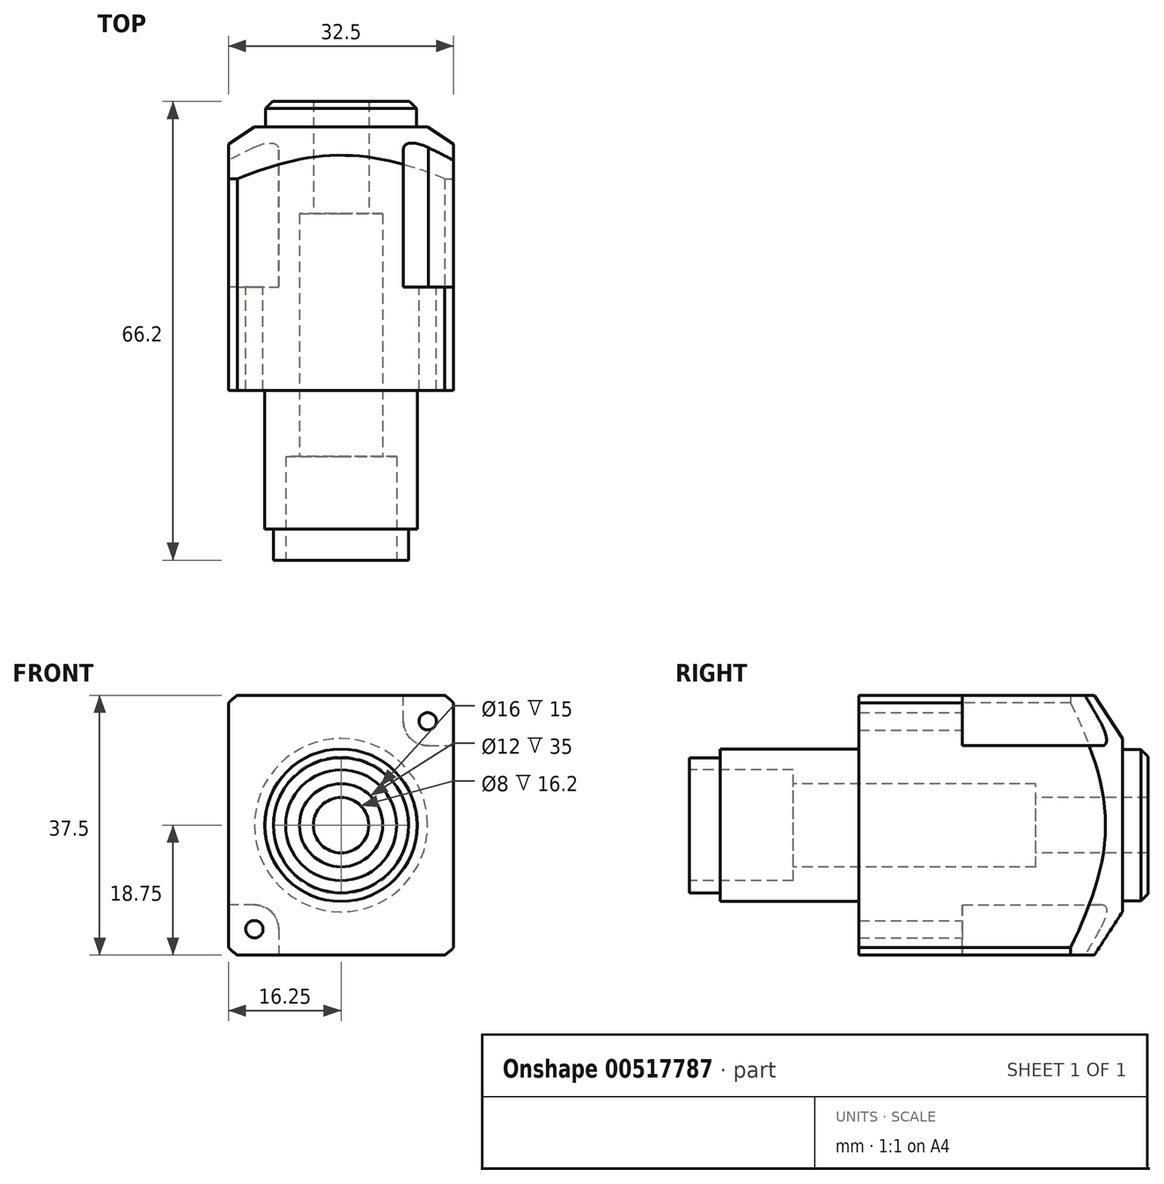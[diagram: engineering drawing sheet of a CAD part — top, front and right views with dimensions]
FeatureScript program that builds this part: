
annotation { "Feature Type Name" : "Feature", "Feature Type Description" : "" }
export const myFeature = defineFeature(function(context is Context, id is Id, definition is map)
    precondition{}
    {
        {
            var Q0;
            Q0=qCreatedBy(makeId("Right.planeOp"),FACE);
            var sketch = newSketch(context, id + "F0", { "sketchPlane" : qUnion([Q0])});
            skLineSegment(sketch, "E0", {"start": v(4.5, 11) * mm, "end": v(24.5, 11) * mm});
            skLineSegment(sketch, "E1", {"start": v(24.5, 24) * mm, "end": v(24.5, 11) * mm});
            skLineSegment(sketch, "E2", {"start": v(24.5, 24) * mm, "end": v(55.03, 24) * mm});
            skLineSegment(sketch, "E3", {"start": v(55.03, 24) * mm, "end": v(62.5, 12.5) * mm});
            skLineSegment(sketch, "E4", {"start": v(66.2, 4) * mm, "end": v(50, 4) * mm});
            skLineSegment(sketch, "E5", {"start": v(50, 4) * mm, "end": v(50, 6) * mm});
            skLineSegment(sketch, "E6", {"start": v(50, 6) * mm, "end": v(15, 6) * mm});
            skLineSegment(sketch, "E7", {"start": v(15, 6) * mm, "end": v(15, 8) * mm});
            skLineSegment(sketch, "E8", {"start": v(15, 8) * mm, "end": v(0, 8) * mm});
            skLineSegment(sketch, "E9", {"start": v(0, 9.75) * mm, "end": v(0, 8) * mm});
            skLineSegment(sketch, "E10", {"start": v(0, 0) * mm, "end": v(89.53, 0) * mm});
            skLineSegment(sketch, "E11", {"start": v(4.5, 11) * mm, "end": v(4.5, 9.75) * mm});
            skPoint(sketch, "E12.orphan", {"position": v(0, 11) * mm});
            skLineSegment(sketch, "E13", {"start": v(66.2, 10.9) * mm, "end": v(66.2, 4) * mm});
            skLineSegment(sketch, "E14", {"start": v(62.5, 12.5) * mm, "end": v(62.5, 10.9) * mm});
            skLineSegment(sketch, "E15", {"start": v(66.2, 10.9) * mm, "end": v(62.5, 10.9) * mm});
            skLineSegment(sketch, "E16", {"start": v(0, 9.75) * mm, "end": v(4.5, 9.75) * mm});
            skSolve(sketch);
        }
        {
            var Q0;
            Q0=makeQuery(id+"F0.imprint","IMPRINT",FACE,{"disambiguationData":[TD([[makeQuery(id+"F0.imprint","IMPRINT",EDGE,{"derivedFrom":sQuery(id+"F0.wireOp",EDGE,"E0")}),-1.0]])]});
            var Q1;
            Q1=sQuery(id+"F0.wireOp",EDGE,"E10");
            revolve(context, id + "F1", {"entities" : qUnion([Q0]), "axis" : qUnion([Q1]), "revolveType" : RevolveType.FULL});
        }
        {
            var Q0;
            Q0=makeQuery(id+"F1.opRevolve","SWEPT_FACE",FACE,{"disambiguationData":[OSD([sQuery(id+"F0.wireOp",EDGE,"E13")])]});
            var sketch = newSketch(context, id + "F2", { "sketchPlane" : qUnion([Q0])});
            skLineSegment(sketch, "E17.bottom", {"start": v(-16.25, 18.75) * mm, "end": v(16.25, 18.75) * mm});
            skLineSegment(sketch, "E17.top", {"start": v(-16.25, -18.75) * mm, "end": v(16.25, -18.75) * mm});
            skLineSegment(sketch, "E17.left", {"start": v(-16.25, 18.75) * mm, "end": v(-16.25, -18.75) * mm});
            skLineSegment(sketch, "E17.right", {"start": v(16.25, 18.75) * mm, "end": v(16.25, -18.75) * mm});
            skLineSegment(sketch, "E18.bottom", {"start": v(-37.96, 36.73) * mm, "end": v(41.17, 36.73) * mm});
            skLineSegment(sketch, "E18.top", {"start": v(-37.96, -41.68) * mm, "end": v(41.17, -41.68) * mm});
            skLineSegment(sketch, "E18.left", {"start": v(-37.96, 36.73) * mm, "end": v(-37.96, -41.68) * mm});
            skLineSegment(sketch, "E18.right", {"start": v(41.17, 36.73) * mm, "end": v(41.17, -41.68) * mm});
            skSolve(sketch);
        }
        {
            var Q0;
            Q0 = qSketchRegion(id + "F2", true);
            extrude(context, id + "F3", {"entities" : qUnion([Q0]), "operationType" : NewBodyOperationType.REMOVE, "endBound" : BoundingType.THROUGH_ALL, "oppositeDirection" : true, "depth" : 25 * mm, "offsetDistance" : 25 * mm});
        }
        {
            var Q0;
            Q0=makeQuery(id+"F1.opRevolve","SWEPT_FACE",FACE,{"disambiguationData":[OSD([sQuery(id+"F0.wireOp",EDGE,"E13")])]});
            var sketch = newSketch(context, id + "F4", { "sketchPlane" : qUnion([Q0])});
            skArc(sketch, "E19", {"start": v(-12.6, 11.5) * mm, "mid": v(-10.06, 12.5) * mm, "end": v(-9, 15) * mm});
            skLineSegment(sketch, "E20", {"start": v(-9, 15) * mm, "end": v(-9, 21) * mm});
            skLineSegment(sketch, "E21", {"start": v(-9, 21) * mm, "end": v(-18, 21) * mm});
            skLineSegment(sketch, "E22", {"start": v(-18, 21) * mm, "end": v(-18, 11.5) * mm});
            skLineSegment(sketch, "E23", {"start": v(-12.6, 11.5) * mm, "end": v(-18, 11.5) * mm});
            skArc(sketch, "E24", {"start": v(12.5, -11.5) * mm, "mid": v(10.03, -12.53) * mm, "end": v(9, -15) * mm});
            skLineSegment(sketch, "E25", {"start": v(12.5, -11.5) * mm, "end": v(18, -11.5) * mm});
            skLineSegment(sketch, "E26", {"start": v(18, -11.5) * mm, "end": v(18, -21) * mm});
            skLineSegment(sketch, "E27", {"start": v(18, -21) * mm, "end": v(9, -21) * mm});
            skLineSegment(sketch, "E28", {"start": v(9, -15) * mm, "end": v(9, -21) * mm});
            skPoint(sketch, "E29.orphan", {"position": v(8.56, -21) * mm});
            skSolve(sketch);
        }
        {
            var Q0;
            Q0 = qSketchRegion(id + "F4", true);
            extrude(context, id + "F5", {"entities" : qUnion([Q0]), "operationType" : NewBodyOperationType.REMOVE, "oppositeDirection" : true, "depth" : 26.8 * mm, "offsetDistance" : 25 * mm});
        }
        {
            var Q0;
            Q0=makeQuery(id+"F5.boolean.opBoolean","COPY",FACE,{"derivedFrom":makeQuery(id+"F5.opExtrude","CAP_FACE",FACE,{"disambiguationData":[OSD([sQuery(id+"F4.wireOp",EDGE,"E24"),sQuery(id+"F4.wireOp",EDGE,"E25"),sQuery(id+"F4.wireOp",EDGE,"E26"),sQuery(id+"F4.wireOp",EDGE,"E27"),sQuery(id+"F4.wireOp",EDGE,"E28")])],"isStart":false})});
            var sketch = newSketch(context, id + "F6", { "sketchPlane" : qUnion([Q0])});
            skPoint(sketch, "E30", {"position": v(-12.5, 15) * mm});
            skPoint(sketch, "E31", {"position": v(12.5, -15) * mm});
            skSolve(sketch);
        }
        {
            var Q0;
            Q0=sQuery(id+"F6.wireOp",VERTEX,"E30");
            var Q1;
            Q1=sQuery(id+"F6.wireOp",VERTEX,"E31");
            var Q2;
            Q2=makeQuery(id+"F1.opRevolve","SWEPT_BODY",BODY,{"disambiguationData":[OSD([sQuery(id+"F0.wireOp",EDGE,"E0"),sQuery(id+"F0.wireOp",EDGE,"E1"),sQuery(id+"F0.wireOp",EDGE,"E2"),sQuery(id+"F0.wireOp",EDGE,"E3"),sQuery(id+"F0.wireOp",EDGE,"E4"),sQuery(id+"F0.wireOp",EDGE,"E5"),sQuery(id+"F0.wireOp",EDGE,"E6"),sQuery(id+"F0.wireOp",EDGE,"E7"),sQuery(id+"F0.wireOp",EDGE,"E8"),sQuery(id+"F0.wireOp",EDGE,"E9"),sQuery(id+"F0.wireOp",EDGE,"TxGgKCIe-eiSN-omVE-WW9B-d0bGM8mBuf6P"),sQuery(id+"F0.wireOp",EDGE,"E11"),sQuery(id+"F0.wireOp",EDGE,"E13"),sQuery(id+"F0.wireOp",EDGE,"E14"),sQuery(id+"F0.wireOp",EDGE,"E15")])]});
            hole(context, id + "F7", {"style" : HoleStyle.SIMPLE, "endStyle" : HoleEndStyle.BLIND, "holeDiameter" : 2.5 * mm, "holeDepth" : 50 * mm, "isTappedThrough" : true, "tappedDepth" : 12 * mm, "tapClearance" : 3, "startFromSketch" : true, "locations" : qUnion([Q0, Q1]), "scope" : qUnion([Q2])});
        }
        {
            var Q0;
            Q0=makeQuery(id+"F1.opRevolve","SWEPT_EDGE",EDGE,{"disambiguationData":[OSD([sQuery(id+"F0.wireOp",EDGE,"E13"),sQuery(id+"F0.wireOp",EDGE,"E15")])]});
            chamfer(context, id + "F8", {"entities" : qUnion([Q0]), "width" : 1 * mm, "tangentPropagation" : true});
        }
    });
